MODEL slx_a12196da3c27
KIND model
CONFIG AbsTol = auto
CONFIG EnableMultiTasking = off
CONFIG FixedStep = auto
CONFIG MaxStep = auto
CONFIG MinStep = auto
CONFIG RelTol = 1e-3
CONFIG SampleTimeConstraint = Unconstrained
CONFIG SolverName = VariableStepAuto
CONFIG StartTime = 0.0
CONFIG StopTime = inf
BLOCK [DataTypeConversion] Cast1
  OutDataTypeStr = int16
  RndMeth = Floor
  SaturateOnIntegerOverflow = off
BLOCK [DataTypeConversion] Cast2
  OutDataTypeStr = int16
  RndMeth = Floor
  SaturateOnIntegerOverflow = off
BLOCK [DataTypeConversion] Cast3
  OutDataTypeStr = int16
  RndMeth = Floor
  SaturateOnIntegerOverflow = off
BLOCK [DataTypeConversion] Cast4
  OutDataTypeStr = int8
  RndMeth = Floor
  SaturateOnIntegerOverflow = off
BLOCK [DataTypeConversion] Cast5
  OutDataTypeStr = uint16
  OutMax = 65535
  OutMin = 0
  RndMeth = Floor
  SaturateOnIntegerOverflow = off
BLOCK [CustomWebBlock] Circular Gauge
  Configuration = {"components":[{"name":"CircularScaleComponent","settings":{"bounds":{"max":1023,"min":0,"tickInterval":100},"direction":"cw","flipLimits":0,"innerRadius":0.75,"internalTickHeightScaleFactor":1,"labelColor":[0,0,0],"labelFont":{"font":"Arial","fontSize":12},"labelRadius":0.6,"labelTransparency":1,"minorTickHeightScaleFactor":0.2,"needleImage":{"size":[200,50],"src":"data:image\/svg+xml;base64,PD94...<+2323ch>
  LabelPosition = Hide
  ShowInitialText = on
BLOCK [CustomTuningWebBlock] Knob
  Configuration = {"components":[{"name":"CircularScaleComponent","settings":{"bounds":{"max":1023,"min":0,"tickInterval":100},"direction":"cw","flipLimits":0,"innerRadius":0.6636618227670849,"internalTickHeightScaleFactor":1,"labelColor":[0,0,0],"labelFont":{"font":"Arial","fontSize":12},"labelRadius":0.84,"labelTransparency":1,"minorTickHeightScaleFactor":0.2,"needleImage":{"size":[150,150],"src":"data:image\/svg...<+39064ch>
  LabelPosition = Hide
  ShowInitialText = on
BLOCK [Display] Load (%)
  Decimation = 1
BLOCK [Gain] Multiply1
  Gain = 0.229
  OutDataTypeStr = double
BLOCK [Gain] Multiply2
  Gain = 0.1
  OutDataTypeStr = double
BLOCK [Display] Position [pulse]
  Decimation = 1
BLOCK [Display] Position [pulse]1
  Decimation = 1
BLOCK [Reference] Read  REF=dxlSimLibrary/Read
  SourceBlock = dxlSimLibrary/Read
  SourceType = Dynamixel Library for MATLAB and Simulink
BLOCK [Reference] Read1  REF=dxlSimLibrary/Read
  SourceBlock = dxlSimLibrary/Read
  SourceType = Dynamixel Library for MATLAB and Simulink
BLOCK [Reference] Read2  REF=dxlSimLibrary/Read
  SourceBlock = dxlSimLibrary/Read
  SourceType = Dynamixel Library for MATLAB and Simulink
BLOCK [Reference] Read3  REF=dxlSimLibrary/Read
  SourceBlock = dxlSimLibrary/Read
  SourceType = Dynamixel Library for MATLAB and Simulink
BLOCK [Reference] Sync Write1  REF=dxlSimLibrary/Sync Write
  SourceBlock = dxlSimLibrary/Sync Write
  SourceType = Dynamixel Library for MATLAB and Simulink
BLOCK [Constant] Target Position
  OutDataTypeStr = int32
  Value = 327.3496779005749
BLOCK [Display] Temperature (oC)
  Decimation = 1
  Format = long
BLOCK [Display] Velocity (rpm)
  Decimation = 1
ANNOTATION (root): Dynamixel library for MATLAB and Simulink Example code - Read/SyncWrite for 1 Dynamixel Motor under Protocol 1.0 Author: Georgios Andrikopoulos (<email>), 2022 Mechatronics & Embedded Control Systems Unit, KTH, Stockholm
LINE Cast1:1 -> Multiply1:1
LINE Cast2:1 -> Position [pulse]:1
LINE Cast3:1 -> Multiply2:1
LINE Cast4:1 -> Temperature (oC):1
LINE Cast5:1 -> Sync Write1:1
LINE Multiply1:1 -> Velocity (rpm):1
LINE Multiply2:1 -> Load (%):1
LINE Read1:1 -> Cast1:1
LINE Read2:1 -> Cast3:1
LINE Read3:1 -> Cast4:1
LINE Read:1 -> Cast2:1
NET Target Position:1 -> Cast5:1, Position [pulse]1:1
note: NET lines group one-source signal fan-out (src -> all destinations, sorted); 1:1 wires keep LINE
